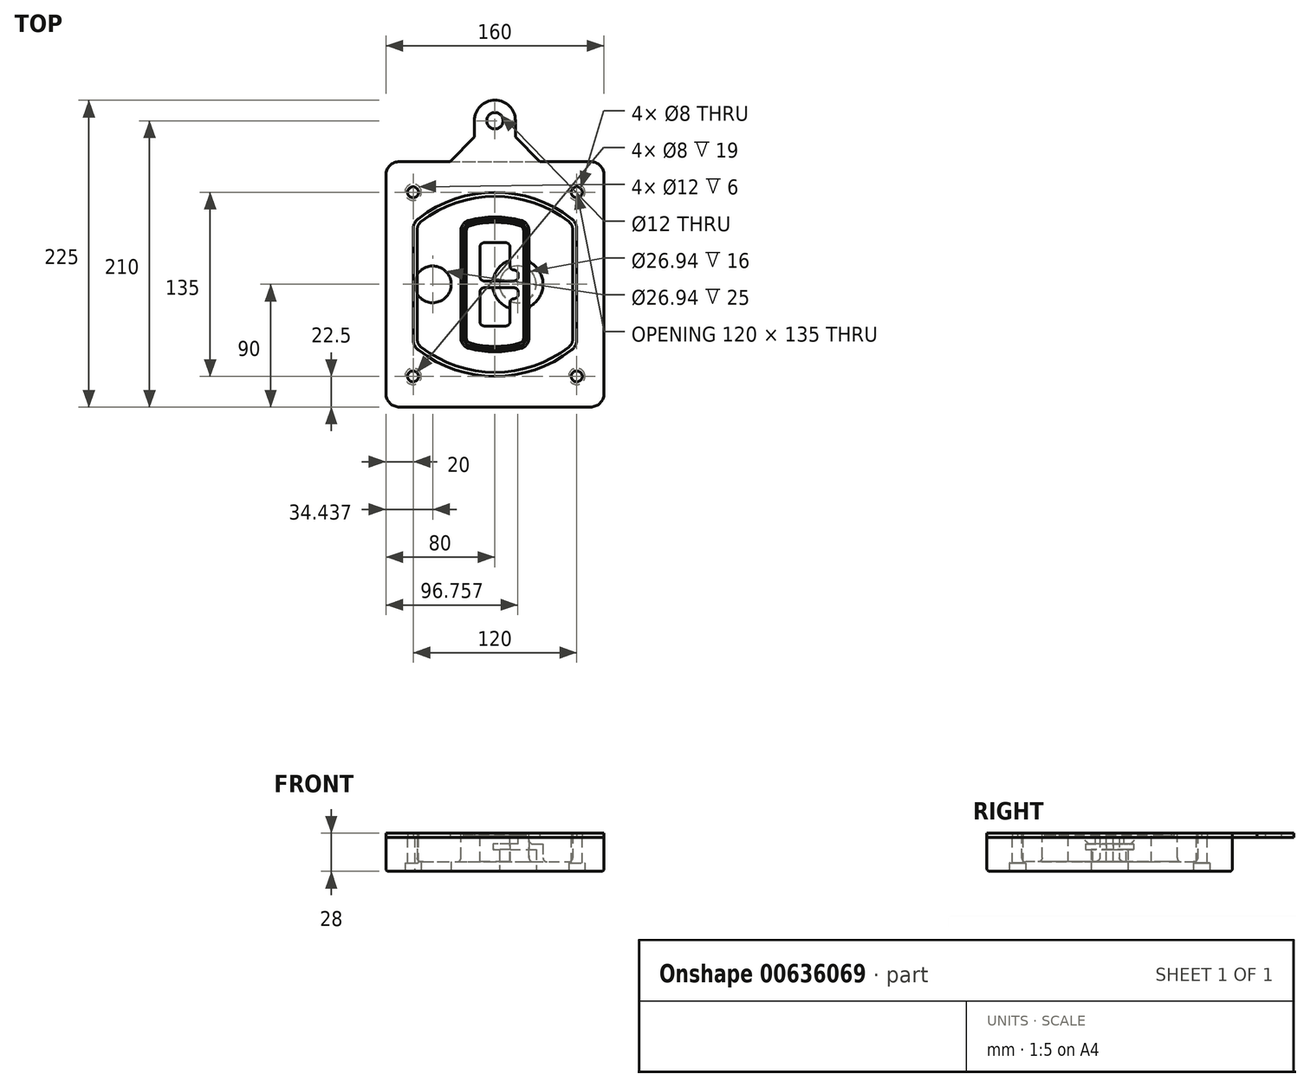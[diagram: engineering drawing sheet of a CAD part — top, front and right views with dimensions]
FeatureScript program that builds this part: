
annotation { "Feature Type Name" : "Feature", "Feature Type Description" : "" }
export const myFeature = defineFeature(function(context is Context, id is Id, definition is map)
    precondition{}
    {
        {
            var Q0;
            Q0=qCreatedBy(makeId("Top.planeOp"),FACE);
            var sketch = newSketch(context, id + "F0", { "sketchPlane" : qUnion([Q0])});
            skPoint(sketch, "E0.rect.middle", {"position": v(0, 0) * mm});
            skLineSegment(sketch, "E1.bottom", {"start": v(-70, -90) * mm, "end": v(70, -90) * mm});
            skLineSegment(sketch, "E1.top", {"start": v(-70, 90) * mm, "end": v(70, 90) * mm});
            skLineSegment(sketch, "E1.left", {"start": v(-80, -80) * mm, "end": v(-80, 80) * mm});
            skLineSegment(sketch, "E1.right", {"start": v(80, -80) * mm, "end": v(80, 80) * mm});
            skLineSegment(sketch, "E2", {"start": v(-80, 90) * mm, "end": v(80, -90) * mm, "construction": true});
            skLineSegment(sketch, "E3", {"start": v(80, 90) * mm, "end": v(-80, -90) * mm, "construction": true});
            skCircle(sketch, "E4", {"center": v(-60, 67.5) * mm, "radius": 4 * mm});
            skCircle(sketch, "E5", {"center": v(60, 67.5) * mm, "radius": 4 * mm});
            skCircle(sketch, "E6", {"center": v(60, -67.5) * mm, "radius": 4 * mm});
            skCircle(sketch, "E7", {"center": v(-60, -67.5) * mm, "radius": 4 * mm});
            skLineSegment(sketch, "E8", {"start": v(-60, 67.5) * mm, "end": v(60, 67.5) * mm, "construction": true});
            skLineSegment(sketch, "E9", {"start": v(60, 67.5) * mm, "end": v(60, -67.5) * mm, "construction": true});
            skLineSegment(sketch, "E10", {"start": v(60, -67.5) * mm, "end": v(-60, -67.5) * mm, "construction": true});
            skLineSegment(sketch, "E11", {"start": v(-60, -67.5) * mm, "end": v(-60, 67.5) * mm, "construction": true});
            skLineSegment(sketch, "E12", {"start": v(-60, 40.3) * mm, "end": v(-60, -40.3) * mm});
            skLineSegment(sketch, "E13", {"start": v(60, 40.3) * mm, "end": v(60, -40.3) * mm});
            skArc(sketch, "E14", {"start": v(56.15, 48.18) * mm, "mid": v(0, 67.5) * mm, "end": v(-56.15, 48.18) * mm});
            skArc(sketch, "E15", {"start": v(-56.15, -48.18) * mm, "mid": v(0, -67.5) * mm, "end": v(56.15, -48.18) * mm});
            skLineSegment(sketch, "E16", {"start": v(-60, 0) * mm, "end": v(60, 0) * mm, "construction": true});
            skPoint(sketch, "E17.visualSharp", {"position": v(-60, -45) * mm});
            skArc(sketch, "E17.filletArc", {"start": v(-60, -40.3) * mm, "mid": v(-58.99, -44.68) * mm, "end": v(-56.15, -48.18) * mm});
            skPoint(sketch, "E18.visualSharp", {"position": v(-60, 45) * mm});
            skArc(sketch, "E18.filletArc", {"start": v(-56.15, 48.18) * mm, "mid": v(-58.99, 44.68) * mm, "end": v(-60, 40.3) * mm});
            skPoint(sketch, "E19.visualSharp", {"position": v(60, 45) * mm});
            skArc(sketch, "E19.filletArc", {"start": v(60, 40.3) * mm, "mid": v(58.99, 44.68) * mm, "end": v(56.15, 48.18) * mm});
            skPoint(sketch, "E20.visualSharp", {"position": v(60, -45) * mm});
            skArc(sketch, "E20.filletArc", {"start": v(56.15, -48.18) * mm, "mid": v(58.99, -44.68) * mm, "end": v(60, -40.3) * mm});
            skPoint(sketch, "E21.visualSharp", {"position": v(-80, 90) * mm});
            skArc(sketch, "E21.filletArc", {"start": v(-70, 90) * mm, "mid": v(-77.07, 87.07) * mm, "end": v(-80, 80) * mm});
            skPoint(sketch, "E22.visualSharp", {"position": v(80, 90) * mm});
            skArc(sketch, "E22.filletArc", {"start": v(80, 80) * mm, "mid": v(77.07, 87.07) * mm, "end": v(70, 90) * mm});
            skPoint(sketch, "E23.visualSharp", {"position": v(80, -90) * mm});
            skArc(sketch, "E23.filletArc", {"start": v(70, -90) * mm, "mid": v(77.07, -87.07) * mm, "end": v(80, -80) * mm});
            skPoint(sketch, "E24.visualSharp", {"position": v(-80, -90) * mm});
            skArc(sketch, "E24.filletArc", {"start": v(-80, -80) * mm, "mid": v(-77.07, -87.07) * mm, "end": v(-70, -90) * mm});
            skArc(sketch, "E25.0", {"start": v(57, 40.3) * mm, "mid": v(56.3, 43.36) * mm, "end": v(54.3, 45.81) * mm});
            skLineSegment(sketch, "E25.1", {"start": v(57, 40.3) * mm, "end": v(57, -40.3) * mm});
            skArc(sketch, "E25.2", {"start": v(54.3, -45.81) * mm, "mid": v(56.3, -43.36) * mm, "end": v(57, -40.3) * mm});
            skArc(sketch, "E25.3", {"start": v(-54.3, -45.81) * mm, "mid": v(0, -64.5) * mm, "end": v(54.3, -45.81) * mm});
            skArc(sketch, "E25.4", {"start": v(-57, -40.3) * mm, "mid": v(-56.3, -43.36) * mm, "end": v(-54.3, -45.81) * mm});
            skArc(sketch, "E25.5", {"start": v(54.3, 45.81) * mm, "mid": v(0, 64.5) * mm, "end": v(-54.3, 45.81) * mm});
            skLineSegment(sketch, "E25.6", {"start": v(-57, 40.3) * mm, "end": v(-57, -40.3) * mm});
            skArc(sketch, "E25.7", {"start": v(-54.3, 45.81) * mm, "mid": v(-56.3, 43.36) * mm, "end": v(-57, 40.3) * mm});
            skArc(sketch, "E26.0", {"start": v(-58.62, 51.33) * mm, "mid": v(-62.58, 46.43) * mm, "end": v(-64, 40.3) * mm});
            skArc(sketch, "E26.1", {"start": v(58.62, 51.33) * mm, "mid": v(0, 71.5) * mm, "end": v(-58.62, 51.33) * mm});
            skArc(sketch, "E26.2", {"start": v(64, 40.3) * mm, "mid": v(62.58, 46.43) * mm, "end": v(58.62, 51.33) * mm});
            skLineSegment(sketch, "E26.3", {"start": v(64, 40.3) * mm, "end": v(64, -40.3) * mm});
            skArc(sketch, "E26.4", {"start": v(58.62, -51.33) * mm, "mid": v(62.58, -46.43) * mm, "end": v(64, -40.3) * mm});
            skLineSegment(sketch, "E26.5", {"start": v(-64, 40.3) * mm, "end": v(-64, -40.3) * mm});
            skArc(sketch, "E26.6", {"start": v(-58.62, -51.33) * mm, "mid": v(0, -71.5) * mm, "end": v(58.62, -51.33) * mm});
            skArc(sketch, "E26.7", {"start": v(-64, -40.3) * mm, "mid": v(-62.58, -46.43) * mm, "end": v(-58.62, -51.33) * mm});
            skSolve(sketch);
        }
        {
            var Q0;
            Q0=makeQuery(id+"F0.imprint","IMPRINT",FACE,{"disambiguationData":[TD([[makeQuery(id+"F0.imprint","IMPRINT",EDGE,{"derivedFrom":sQuery(id+"F0.wireOp",EDGE,"E1.bottom")}),1.0]])]});
            var Q1;
            Q1=makeQuery(id+"F0.imprint","IMPRINT",FACE,{"disambiguationData":[TD([[makeQuery(id+"F0.imprint","IMPRINT",EDGE,{"derivedFrom":sQuery(id+"F0.wireOp",EDGE,"E12")}),1.0]])]});
            var Q2;
            Q2=makeQuery(id+"F0.imprint","IMPRINT",FACE,{"disambiguationData":[TD([[makeQuery(id+"F0.imprint","IMPRINT",EDGE,{"derivedFrom":sQuery(id+"F0.wireOp",EDGE,"E25.0")}),1.0]])]});
            var Q3;
            Q3=makeQuery(id+"F0.imprint","IMPRINT",FACE,{"disambiguationData":[TD([[makeQuery(id+"F0.imprint","IMPRINT",EDGE,{"derivedFrom":sQuery(id+"F0.wireOp",EDGE,"E12")}),-1.0]])]});
            extrude(context, id + "F1", {"entities" : qUnion([Q0, Q1, Q2, Q3]), "oppositeDirection" : true, "depth" : 25 * mm});
        }
        {
            var Q0;
            Q0=makeQuery(id+"F0.imprint","IMPRINT",FACE,{"disambiguationData":[TD([[makeQuery(id+"F0.imprint","IMPRINT",EDGE,{"derivedFrom":sQuery(id+"F0.wireOp",EDGE,"E12")}),1.0]])]});
            extrude(context, id + "F2", {"entities" : qUnion([Q0]), "operationType" : NewBodyOperationType.ADD, "depth" : 3 * mm});
        }
        {
            var Q0;
            Q0=makeQuery(id+"F0.imprint","IMPRINT",FACE,{"disambiguationData":[TD([[makeQuery(id+"F0.imprint","IMPRINT",EDGE,{"derivedFrom":sQuery(id+"F0.wireOp",EDGE,"E25.0")}),1.0]])]});
            extrude(context, id + "F3", {"entities" : qUnion([Q0]), "operationType" : NewBodyOperationType.REMOVE, "oppositeDirection" : true, "depth" : 18 * mm});
        }
        {
            var Q0;
            Q0=makeQuery(id+"F2.opExtrude","CAP_FACE",FACE,{"disambiguationData":[OSD([sQuery(id+"F0.wireOp",EDGE,"E12"),sQuery(id+"F0.wireOp",EDGE,"E13"),sQuery(id+"F0.wireOp",EDGE,"E14"),sQuery(id+"F0.wireOp",EDGE,"E15"),sQuery(id+"F0.wireOp",EDGE,"E17.filletArc"),sQuery(id+"F0.wireOp",EDGE,"E18.filletArc"),sQuery(id+"F0.wireOp",EDGE,"E19.filletArc"),sQuery(id+"F0.wireOp",EDGE,"E20.filletArc"),sQuery(id+"F0.wireOp",EDGE,"E25.0"),sQuery(id+"F0.wireOp",EDGE,"E25.1"),sQuery(id+"F0.wireOp",EDGE,"E25.2"),sQuery(id+"F0.wireOp",EDGE,"E25.3"),sQuery(id+"F0.wireOp",EDGE,"E25.4"),sQuery(id+"F0.wireOp",EDGE,"E25.5"),sQuery(id+"F0.wireOp",EDGE,"E25.6"),sQuery(id+"F0.wireOp",EDGE,"E25.7")])],"isStart":false});
            var sketch = newSketch(context, id + "F4", { "sketchPlane" : qUnion([Q0])});
            skArc(sketch, "E27.0", {"start": v(-19.08, -46.97) * mm, "mid": v(0, -49.5) * mm, "end": v(19.08, -46.97) * mm});
            skArc(sketch, "E28.0", {"start": v(19.08, 46.97) * mm, "mid": v(0, 49.5) * mm, "end": v(-19.08, 46.97) * mm});
            skLineSegment(sketch, "E29", {"start": v(-25, 39.25) * mm, "end": v(-25, -39.25) * mm});
            skLineSegment(sketch, "E30", {"start": v(25, 39.25) * mm, "end": v(25, -39.25) * mm});
            skLineSegment(sketch, "E31", {"start": v(-25, 45.1) * mm, "end": v(25, 45.1) * mm, "construction": true});
            skLineSegment(sketch, "E32", {"start": v(-25, -45.1) * mm, "end": v(25, -45.1) * mm, "construction": true});
            skPoint(sketch, "E33.visualSharp", {"position": v(-25, 45.1) * mm});
            skArc(sketch, "E33.filletArc", {"start": v(-19.08, 46.97) * mm, "mid": v(-23.35, 44.11) * mm, "end": v(-25, 39.25) * mm});
            skPoint(sketch, "E34.visualSharp", {"position": v(25, 45.1) * mm});
            skArc(sketch, "E34.filletArc", {"start": v(25, 39.25) * mm, "mid": v(23.35, 44.11) * mm, "end": v(19.08, 46.97) * mm});
            skPoint(sketch, "E35.visualSharp", {"position": v(25, -45.1) * mm});
            skArc(sketch, "E35.filletArc", {"start": v(19.08, -46.97) * mm, "mid": v(23.35, -44.11) * mm, "end": v(25, -39.25) * mm});
            skPoint(sketch, "E36.visualSharp", {"position": v(-25, -45.1) * mm});
            skArc(sketch, "E36.filletArc", {"start": v(-25, -39.25) * mm, "mid": v(-23.35, -44.11) * mm, "end": v(-19.08, -46.97) * mm});
            skArc(sketch, "E37.0", {"start": v(54.3, 45.81) * mm, "mid": v(0, 64.5) * mm, "end": v(-54.3, 45.81) * mm});
            skArc(sketch, "E37.1", {"start": v(-54.3, 45.81) * mm, "mid": v(-56.3, 43.36) * mm, "end": v(-57, 40.3) * mm});
            skLineSegment(sketch, "E37.2", {"start": v(-57, 40.3) * mm, "end": v(-57, -40.3) * mm});
            skArc(sketch, "E37.3", {"start": v(-57, -40.3) * mm, "mid": v(-56.3, -43.36) * mm, "end": v(-54.3, -45.81) * mm});
            skArc(sketch, "E37.4", {"start": v(-54.3, -45.81) * mm, "mid": v(0, -64.5) * mm, "end": v(54.3, -45.81) * mm});
            skArc(sketch, "E37.5", {"start": v(54.3, -45.81) * mm, "mid": v(56.3, -43.36) * mm, "end": v(57, -40.3) * mm});
            skLineSegment(sketch, "E37.6", {"start": v(57, 40.3) * mm, "end": v(57, -40.3) * mm});
            skArc(sketch, "E37.7", {"start": v(57, 40.3) * mm, "mid": v(56.3, 43.36) * mm, "end": v(54.3, 45.81) * mm});
            skLineSegment(sketch, "E38.0", {"start": v(23, 39.25) * mm, "end": v(23, -39.25) * mm});
            skArc(sketch, "E38.1", {"start": v(18.56, -45.04) * mm, "mid": v(21.76, -42.9) * mm, "end": v(23, -39.25) * mm});
            skArc(sketch, "E38.2", {"start": v(-18.56, -45.04) * mm, "mid": v(0, -47.5) * mm, "end": v(18.56, -45.04) * mm});
            skArc(sketch, "E38.3", {"start": v(-23, -39.25) * mm, "mid": v(-21.76, -42.9) * mm, "end": v(-18.56, -45.04) * mm});
            skLineSegment(sketch, "E38.4", {"start": v(-23, 39.25) * mm, "end": v(-23, -39.25) * mm});
            skArc(sketch, "E38.5", {"start": v(23, 39.25) * mm, "mid": v(21.76, 42.9) * mm, "end": v(18.56, 45.04) * mm});
            skArc(sketch, "E38.6", {"start": v(-18.56, 45.04) * mm, "mid": v(-21.76, 42.9) * mm, "end": v(-23, 39.25) * mm});
            skArc(sketch, "E38.7", {"start": v(18.56, 45.04) * mm, "mid": v(0, 47.5) * mm, "end": v(-18.56, 45.04) * mm});
            skArc(sketch, "E39.0", {"start": v(21, 39.25) * mm, "mid": v(20.18, 41.68) * mm, "end": v(18.04, 43.1) * mm});
            skLineSegment(sketch, "E39.1", {"start": v(21, 39.25) * mm, "end": v(21, -39.25) * mm});
            skArc(sketch, "E39.2", {"start": v(18.04, -43.1) * mm, "mid": v(20.18, -41.68) * mm, "end": v(21, -39.25) * mm});
            skArc(sketch, "E39.3", {"start": v(-18.04, -43.1) * mm, "mid": v(0, -45.5) * mm, "end": v(18.04, -43.1) * mm});
            skArc(sketch, "E39.4", {"start": v(-21, -39.25) * mm, "mid": v(-20.18, -41.68) * mm, "end": v(-18.04, -43.1) * mm});
            skArc(sketch, "E39.5", {"start": v(18.04, 43.1) * mm, "mid": v(0, 45.5) * mm, "end": v(-18.04, 43.1) * mm});
            skLineSegment(sketch, "E39.6", {"start": v(-21, 39.25) * mm, "end": v(-21, -39.25) * mm});
            skArc(sketch, "E39.7", {"start": v(-18.04, 43.1) * mm, "mid": v(-20.18, 41.68) * mm, "end": v(-21, 39.25) * mm});
            skLineSegment(sketch, "E40", {"start": v(-25, 0) * mm, "end": v(25, 0) * mm, "construction": true});
            skLineSegment(sketch, "E41", {"start": v(-11, 5.5) * mm, "end": v(-11, 27.5) * mm});
            skLineSegment(sketch, "E42", {"start": v(-8, 30.5) * mm, "end": v(8, 30.5) * mm});
            skLineSegment(sketch, "E43", {"start": v(11, 27.5) * mm, "end": v(11, 13.5) * mm});
            skLineSegment(sketch, "E44", {"start": v(14, 10.5) * mm, "end": v(14, 10.5) * mm});
            skLineSegment(sketch, "E45", {"start": v(17, 7.5) * mm, "end": v(17, 5.5) * mm});
            skLineSegment(sketch, "E46", {"start": v(14, 2.5) * mm, "end": v(-8, 2.5) * mm});
            skPoint(sketch, "E47.visualSharp", {"position": v(-11, 30.5) * mm});
            skArc(sketch, "E47.filletArc", {"start": v(-8, 30.5) * mm, "mid": v(-10.12, 29.62) * mm, "end": v(-11, 27.5) * mm});
            skPoint(sketch, "E48.visualSharp", {"position": v(11, 30.5) * mm});
            skArc(sketch, "E48.filletArc", {"start": v(11, 27.5) * mm, "mid": v(10.12, 29.62) * mm, "end": v(8, 30.5) * mm});
            skPoint(sketch, "E49.visualSharp", {"position": v(11, 10.5) * mm});
            skArc(sketch, "E49.filletArc", {"start": v(11, 13.5) * mm, "mid": v(11.88, 11.38) * mm, "end": v(14, 10.5) * mm});
            skPoint(sketch, "E50.visualSharp", {"position": v(17, 10.5) * mm});
            skArc(sketch, "E50.filletArc", {"start": v(17, 7.5) * mm, "mid": v(16.12, 9.62) * mm, "end": v(14, 10.5) * mm});
            skPoint(sketch, "E51.visualSharp", {"position": v(17, 2.5) * mm});
            skArc(sketch, "E51.filletArc", {"start": v(14, 2.5) * mm, "mid": v(16.12, 3.38) * mm, "end": v(17, 5.5) * mm});
            skPoint(sketch, "E52.visualSharp", {"position": v(-11, 2.5) * mm});
            skArc(sketch, "E52.filletArc", {"start": v(-11, 5.5) * mm, "mid": v(-10.12, 3.38) * mm, "end": v(-8, 2.5) * mm});
            skLineSegment(sketch, "E53.0.MirrorCS", {"start": v(14, -2.5) * mm, "end": v(-8, -2.5) * mm});
            skArc(sketch, "E54.0.MirrorCS", {"start": v(-11, -5.5) * mm, "mid": v(-10.12, -3.38) * mm, "end": v(-8, -2.5) * mm});
            skLineSegment(sketch, "E55.0.MirrorCS", {"start": v(-11, -5.5) * mm, "end": v(-11, -27.5) * mm});
            skArc(sketch, "E56.0.MirrorCS", {"start": v(-8, -30.5) * mm, "mid": v(-10.12, -29.62) * mm, "end": v(-11, -27.5) * mm});
            skLineSegment(sketch, "E57.0.MirrorCS", {"start": v(-8, -30.5) * mm, "end": v(8, -30.5) * mm});
            skArc(sketch, "E58.0.MirrorCS", {"start": v(11, -27.5) * mm, "mid": v(10.12, -29.62) * mm, "end": v(8, -30.5) * mm});
            skLineSegment(sketch, "E59.0.MirrorCS", {"start": v(11, -27.5) * mm, "end": v(11, -13.5) * mm});
            skArc(sketch, "E60.0.MirrorCS", {"start": v(11, -13.5) * mm, "mid": v(11.88, -11.38) * mm, "end": v(14, -10.5) * mm});
            skArc(sketch, "E61.0.MirrorCS", {"start": v(17, -7.5) * mm, "mid": v(16.12, -9.62) * mm, "end": v(14, -10.5) * mm});
            skLineSegment(sketch, "E62.0.MirrorCS", {"start": v(17, -7.5) * mm, "end": v(17, -5.5) * mm});
            skArc(sketch, "E63.0.MirrorCS", {"start": v(14, -2.5) * mm, "mid": v(16.12, -3.38) * mm, "end": v(17, -5.5) * mm});
            skSolve(sketch);
        }
        {
            var Q0;
            Q0=makeQuery(id+"F4.imprint","IMPRINT",FACE,{"disambiguationData":[TD([[makeQuery(id+"F4.imprint","IMPRINT",EDGE,{"derivedFrom":sQuery(id+"F4.wireOp",EDGE,"E27.0")}),1.0]])]});
            var Q1;
            Q1=makeQuery(id+"F4.imprint","IMPRINT",FACE,{"disambiguationData":[TD([[makeQuery(id+"F4.imprint","IMPRINT",EDGE,{"derivedFrom":sQuery(id+"F4.wireOp",EDGE,"E38.0")}),-1.0]])]});
            var Q2;
            Q2=makeQuery(id+"F4.imprint","IMPRINT",FACE,{"disambiguationData":[TD([[makeQuery(id+"F4.imprint","IMPRINT",EDGE,{"derivedFrom":sQuery(id+"F4.wireOp",EDGE,"E39.0")}),1.0]])]});
            extrude(context, id + "F5", {"entities" : qUnion([Q0, Q1, Q2]), "operationType" : NewBodyOperationType.ADD, "endBound" : BoundingType.UP_TO_NEXT, "oppositeDirection" : true, "depth" : 25 * mm});
        }
        {
            var Q0;
            Q0=makeQuery(id+"F4.imprint","IMPRINT",FACE,{"disambiguationData":[TD([[makeQuery(id+"F4.imprint","IMPRINT",EDGE,{"derivedFrom":sQuery(id+"F4.wireOp",EDGE,"E38.0")}),-1.0]])]});
            extrude(context, id + "F6", {"entities" : qUnion([Q0]), "operationType" : NewBodyOperationType.REMOVE, "oppositeDirection" : true, "depth" : 2 * mm});
        }
        {
            var Q0;
            Q0=makeQuery(id+"F1.opExtrude","CAP_FACE",FACE,{"disambiguationData":[OSD([sQuery(id+"F0.wireOp",EDGE,"E1.bottom"),sQuery(id+"F0.wireOp",EDGE,"E1.top"),sQuery(id+"F0.wireOp",EDGE,"E1.left"),sQuery(id+"F0.wireOp",EDGE,"E1.right"),sQuery(id+"F0.wireOp",EDGE,"E4"),sQuery(id+"F0.wireOp",EDGE,"E5"),sQuery(id+"F0.wireOp",EDGE,"E6"),sQuery(id+"F0.wireOp",EDGE,"E7"),sQuery(id+"F0.wireOp",EDGE,"E21.filletArc"),sQuery(id+"F0.wireOp",EDGE,"E22.filletArc"),sQuery(id+"F0.wireOp",EDGE,"E23.filletArc"),sQuery(id+"F0.wireOp",EDGE,"E24.filletArc")])],"isStart":false});
            var sketch = newSketch(context, id + "F7", { "sketchPlane" : qUnion([Q0])});
            skCircle(sketch, "E64", {"center": v(16.76, 0) * mm, "radius": 13.47 * mm});
            skCircle(sketch, "E65", {"center": v(-45.56, 0) * mm, "radius": 13.47 * mm});
            skLineSegment(sketch, "E66", {"start": v(80, 0) * mm, "end": v(-80, 0) * mm});
            skCircle(sketch, "E67", {"center": v(16.76, 0) * mm, "radius": 18.47 * mm});
            skCircle(sketch, "E68", {"center": v(60, -67.5) * mm, "radius": 6 * mm});
            skCircle(sketch, "E69", {"center": v(-60, -67.5) * mm, "radius": 6 * mm});
            skCircle(sketch, "E70", {"center": v(-60, 67.5) * mm, "radius": 6 * mm});
            skCircle(sketch, "E71", {"center": v(60, 67.5) * mm, "radius": 6 * mm});
            skSolve(sketch);
        }
        {
            var Q0;
            {var subQ1=sQuery(id+"F7.wireOp",EDGE,"E66");var subQ4=sQuery(id+"F7.wireOp",EDGE,"E64");var subQ6=makeQuery(id+"F7.imprint","INTERSECT",VERTEX,{"disambiguationData":[OD(0.0)],"derivedFrom":[subQ4,subQ1]});Q0=makeQuery(id+"F7.imprint","IMPRINT",FACE,{"disambiguationData":[TD([[makeQuery(id+"F7.imprint","IMPRINT",EDGE,{"disambiguationData":[TD([[subQ6,-1.0]])],"derivedFrom":subQ4}),-1.0]])]});}
            var Q1;
            {var subQ0=sQuery(id+"F7.wireOp",EDGE,"E66");var subQ1=sQuery(id+"F7.wireOp",EDGE,"E64");var subQ3=makeQuery(id+"F7.imprint","INTERSECT",VERTEX,{"disambiguationData":[OD(0.0)],"derivedFrom":[subQ1,subQ0]});Q1=makeQuery(id+"F7.imprint","IMPRINT",FACE,{"disambiguationData":[TD([[makeQuery(id+"F7.imprint","IMPRINT",EDGE,{"disambiguationData":[TD([[subQ3,-1.0]])],"derivedFrom":subQ1}),1.0]])]});}
            var Q2;
            {var subQ0=sQuery(id+"F7.wireOp",EDGE,"E66");var subQ1=sQuery(id+"F7.wireOp",EDGE,"E64");var subQ3=makeQuery(id+"F7.imprint","INTERSECT",VERTEX,{"disambiguationData":[OD(0.0)],"derivedFrom":[subQ1,subQ0]});Q2=makeQuery(id+"F7.imprint","IMPRINT",FACE,{"disambiguationData":[TD([[makeQuery(id+"F7.imprint","IMPRINT",EDGE,{"disambiguationData":[TD([[subQ3,1.0]])],"derivedFrom":subQ1}),1.0]])]});}
            var Q3;
            {var subQ1=sQuery(id+"F7.wireOp",EDGE,"E66");var subQ4=sQuery(id+"F7.wireOp",EDGE,"E64");var subQ6=makeQuery(id+"F7.imprint","INTERSECT",VERTEX,{"disambiguationData":[OD(0.0)],"derivedFrom":[subQ4,subQ1]});Q3=makeQuery(id+"F7.imprint","IMPRINT",FACE,{"disambiguationData":[TD([[makeQuery(id+"F7.imprint","IMPRINT",EDGE,{"disambiguationData":[TD([[subQ6,1.0]])],"derivedFrom":subQ4}),-1.0]])]});}
            extrude(context, id + "F8", {"entities" : qUnion([Q0, Q1, Q2, Q3]), "operationType" : NewBodyOperationType.ADD, "oppositeDirection" : true, "depth" : 20 * mm});
        }
        {
            var Q0;
            {var subQ0=sQuery(id+"F7.wireOp",EDGE,"E66");var subQ1=sQuery(id+"F7.wireOp",EDGE,"E64");var subQ3=makeQuery(id+"F7.imprint","INTERSECT",VERTEX,{"disambiguationData":[OD(0.0)],"derivedFrom":[subQ1,subQ0]});Q0=makeQuery(id+"F7.imprint","IMPRINT",FACE,{"disambiguationData":[TD([[makeQuery(id+"F7.imprint","IMPRINT",EDGE,{"disambiguationData":[TD([[subQ3,-1.0]])],"derivedFrom":subQ1}),1.0]])]});}
            var Q1;
            {var subQ0=sQuery(id+"F7.wireOp",EDGE,"E66");var subQ1=sQuery(id+"F7.wireOp",EDGE,"E64");var subQ3=makeQuery(id+"F7.imprint","INTERSECT",VERTEX,{"disambiguationData":[OD(0.0)],"derivedFrom":[subQ1,subQ0]});Q1=makeQuery(id+"F7.imprint","IMPRINT",FACE,{"disambiguationData":[TD([[makeQuery(id+"F7.imprint","IMPRINT",EDGE,{"disambiguationData":[TD([[subQ3,1.0]])],"derivedFrom":subQ1}),1.0]])]});}
            extrude(context, id + "F9", {"entities" : qUnion([Q0, Q1]), "operationType" : NewBodyOperationType.REMOVE, "oppositeDirection" : true, "depth" : 16 * mm});
        }
        {
            var Q0;
            {var subQ0=sQuery(id+"F7.wireOp",EDGE,"E66");var subQ1=sQuery(id+"F7.wireOp",EDGE,"E65");var subQ3=makeQuery(id+"F7.imprint","INTERSECT",VERTEX,{"disambiguationData":[OD(0.0)],"derivedFrom":[subQ1,subQ0]});Q0=makeQuery(id+"F7.imprint","IMPRINT",FACE,{"disambiguationData":[TD([[makeQuery(id+"F7.imprint","IMPRINT",EDGE,{"disambiguationData":[TD([[subQ3,-1.0]])],"derivedFrom":subQ1}),1.0]])]});}
            var Q1;
            {var subQ0=sQuery(id+"F7.wireOp",EDGE,"E66");var subQ1=sQuery(id+"F7.wireOp",EDGE,"E65");var subQ3=makeQuery(id+"F7.imprint","INTERSECT",VERTEX,{"disambiguationData":[OD(0.0)],"derivedFrom":[subQ1,subQ0]});Q1=makeQuery(id+"F7.imprint","IMPRINT",FACE,{"disambiguationData":[TD([[makeQuery(id+"F7.imprint","IMPRINT",EDGE,{"disambiguationData":[TD([[subQ3,1.0]])],"derivedFrom":subQ1}),1.0]])]});}
            extrude(context, id + "F10", {"entities" : qUnion([Q0, Q1]), "operationType" : NewBodyOperationType.REMOVE, "oppositeDirection" : true, "depth" : 25 * mm});
        }
        {
            var Q0;
            Q0=makeQuery(id+"F7.imprint","IMPRINT",FACE,{"disambiguationData":[TD([[makeQuery(id+"F7.imprint","IMPRINT",EDGE,{"derivedFrom":sQuery(id+"F7.wireOp",EDGE,"E68")}),1.0]])]});
            var Q1;
            Q1=makeQuery(id+"F7.imprint","IMPRINT",FACE,{"disambiguationData":[TD([[makeQuery(id+"F7.imprint","IMPRINT",EDGE,{"derivedFrom":makeQuery(id+"F1.opExtrude","CAP_EDGE",EDGE,{"disambiguationData":[OSD([sQuery(id+"F0.wireOp",EDGE,"E5")])],"isStart":false})}),-1.0]])]});
            var Q2;
            Q2=makeQuery(id+"F7.imprint","IMPRINT",FACE,{"disambiguationData":[TD([[makeQuery(id+"F7.imprint","IMPRINT",EDGE,{"derivedFrom":sQuery(id+"F7.wireOp",EDGE,"E69")}),1.0]])]});
            var Q3;
            Q3=makeQuery(id+"F7.imprint","IMPRINT",FACE,{"disambiguationData":[TD([[makeQuery(id+"F7.imprint","IMPRINT",EDGE,{"derivedFrom":makeQuery(id+"F1.opExtrude","CAP_EDGE",EDGE,{"disambiguationData":[OSD([sQuery(id+"F0.wireOp",EDGE,"E4")])],"isStart":false})}),-1.0]])]});
            var Q4;
            Q4=makeQuery(id+"F7.imprint","IMPRINT",FACE,{"disambiguationData":[TD([[makeQuery(id+"F7.imprint","IMPRINT",EDGE,{"derivedFrom":sQuery(id+"F7.wireOp",EDGE,"E70")}),1.0]])]});
            var Q5;
            Q5=makeQuery(id+"F7.imprint","IMPRINT",FACE,{"disambiguationData":[TD([[makeQuery(id+"F7.imprint","IMPRINT",EDGE,{"derivedFrom":makeQuery(id+"F1.opExtrude","CAP_EDGE",EDGE,{"disambiguationData":[OSD([sQuery(id+"F0.wireOp",EDGE,"E7")])],"isStart":false})}),-1.0]])]});
            var Q6;
            Q6=makeQuery(id+"F7.imprint","IMPRINT",FACE,{"disambiguationData":[TD([[makeQuery(id+"F7.imprint","IMPRINT",EDGE,{"derivedFrom":sQuery(id+"F7.wireOp",EDGE,"E71")}),1.0]])]});
            var Q7;
            Q7=makeQuery(id+"F7.imprint","IMPRINT",FACE,{"disambiguationData":[TD([[makeQuery(id+"F7.imprint","IMPRINT",EDGE,{"derivedFrom":makeQuery(id+"F1.opExtrude","CAP_EDGE",EDGE,{"disambiguationData":[OSD([sQuery(id+"F0.wireOp",EDGE,"E6")])],"isStart":false})}),-1.0]])]});
            extrude(context, id + "F11", {"entities" : qUnion([Q0, Q1, Q2, Q3, Q4, Q5, Q6, Q7]), "operationType" : NewBodyOperationType.REMOVE, "oppositeDirection" : true, "depth" : 6 * mm});
        }
        {
            var Q0;
            Q0=makeQuery(id+"F9.boolean.opBoolean","COPY",FACE,{"derivedFrom":makeQuery(id+"F9.opExtrude","CAP_FACE",FACE,{"disambiguationData":[OSD([sQuery(id+"F7.wireOp",EDGE,"E64")])],"isStart":false})});
            var sketch = newSketch(context, id + "F12", { "sketchPlane" : qUnion([Q0])});
            skArc(sketch, "E72.0", {"start": v(11, 17.55) * mm, "mid": v(2.57, 11.82) * mm, "end": v(-1.54, 2.5) * mm});
            skArc(sketch, "E72.1", {"start": v(-1.54, -2.5) * mm, "mid": v(2.57, -11.82) * mm, "end": v(11, -17.55) * mm});
            skLineSegment(sketch, "E73", {"start": v(-1.54, -2.5) * mm, "end": v(14, -2.5) * mm});
            skLineSegment(sketch, "E74.0", {"start": v(14, 2.5) * mm, "end": v(-1.54, 2.5) * mm});
            skArc(sketch, "E74.1", {"start": v(14, 2.5) * mm, "mid": v(16.12, 3.38) * mm, "end": v(17, 5.5) * mm});
            skLineSegment(sketch, "E74.2", {"start": v(17, 7.5) * mm, "end": v(17, 5.5) * mm});
            skArc(sketch, "E74.3", {"start": v(17, 7.5) * mm, "mid": v(16.12, 9.62) * mm, "end": v(14, 10.5) * mm});
            skArc(sketch, "E74.4", {"start": v(11, 13.5) * mm, "mid": v(11.88, 11.38) * mm, "end": v(14, 10.5) * mm});
            skLineSegment(sketch, "E74.5", {"start": v(11, 17.55) * mm, "end": v(11, 13.5) * mm});
            skLineSegment(sketch, "E74.7", {"start": v(14, -2.5) * mm, "end": v(-1.54, -2.5) * mm});
            skArc(sketch, "E74.8", {"start": v(14, -2.5) * mm, "mid": v(16.12, -3.38) * mm, "end": v(17, -5.5) * mm});
            skLineSegment(sketch, "E74.9", {"start": v(17, -7.5) * mm, "end": v(17, -5.5) * mm});
            skArc(sketch, "E74.10", {"start": v(17, -7.5) * mm, "mid": v(16.12, -9.62) * mm, "end": v(14, -10.5) * mm});
            skArc(sketch, "E74.11", {"start": v(11, -13.5) * mm, "mid": v(11.88, -11.38) * mm, "end": v(14, -10.5) * mm});
            skLineSegment(sketch, "E74.12", {"start": v(11, -17.55) * mm, "end": v(11, -13.5) * mm});
            skPoint(sketch, "E75.orphan", {"position": v(11, -27.5) * mm});
            skPoint(sketch, "E76.orphan", {"position": v(-8, -2.5) * mm});
            skPoint(sketch, "E77.orphan", {"position": v(-8, 2.5) * mm});
            skPoint(sketch, "E78.orphan", {"position": v(11, 27.5) * mm});
            skSolve(sketch);
        }
        {
            var Q0;
            {var subQ7=sQuery(id+"F12.wireOp",EDGE,"E72.0");var subQ14=sQuery(id+"F12.wireOp",EDGE,"E72.1");var subQ16=sQuery(id+"F12.wireOp",EDGE,"E74.1");var subQ18=sQuery(id+"F12.wireOp",EDGE,"E74.8");Q0=qUnion([makeQuery(id+"F12.imprint","IMPRINT",FACE,{"disambiguationData":[TD([[makeQuery(id+"F12.imprint","IMPRINT",EDGE,{"derivedFrom":subQ7}),1.0]])]}),makeQuery(id+"F12.imprint","IMPRINT",FACE,{"disambiguationData":[TD([[makeQuery(id+"F12.imprint","IMPRINT",EDGE,{"derivedFrom":subQ14}),1.0]])]}),makeQuery(id+"F12.imprint","IMPRINT",FACE,{"disambiguationData":[TD([[makeQuery(id+"F12.imprint","IMPRINT",EDGE,{"derivedFrom":subQ16}),1.0]])]}),makeQuery(id+"F12.imprint","IMPRINT",FACE,{"disambiguationData":[TD([[makeQuery(id+"F12.imprint","IMPRINT",EDGE,{"derivedFrom":subQ18}),-1.0]])]})]);}
            var Q1;
            Q1=makeQuery(id+"F5.boolean.opBoolean","SPLIT",FACE,{"disambiguationData":[TD([makeQuery(id+"F5.opExtrude","SWEPT_FACE",FACE,{"disambiguationData":[OSD([sQuery(id+"F4.wireOp",EDGE,"E41")])]})])],"derivedFrom":makeQuery(id+"F3.boolean.opBoolean","COPY",FACE,{"derivedFrom":makeQuery(id+"F3.opExtrude","CAP_FACE",FACE,{"disambiguationData":[OSD([sQuery(id+"F0.wireOp",EDGE,"E25.0"),sQuery(id+"F0.wireOp",EDGE,"E25.1"),sQuery(id+"F0.wireOp",EDGE,"E25.2"),sQuery(id+"F0.wireOp",EDGE,"E25.3"),sQuery(id+"F0.wireOp",EDGE,"E25.4"),sQuery(id+"F0.wireOp",EDGE,"E25.5"),sQuery(id+"F0.wireOp",EDGE,"E25.6"),sQuery(id+"F0.wireOp",EDGE,"E25.7")])],"isStart":false})})});
            extrude(context, id + "F13", {"entities" : qUnion([Q0]), "operationType" : NewBodyOperationType.REMOVE, "endBound" : BoundingType.UP_TO_SURFACE, "endBoundEntityFace" : qUnion([Q1]), "depth" : 25 * mm});
        }
        {
            var Q0;
            Q0=makeQuery(id+"F3.boolean.opBoolean","COPY",EDGE,{"derivedFrom":makeQuery(id+"F3.opExtrude","CAP_EDGE",EDGE,{"disambiguationData":[OSD([sQuery(id+"F0.wireOp",EDGE,"E25.6")])],"isStart":false})});
            var Q1;
            Q1=makeQuery(id+"F8.boolean.opBoolean","INTERSECT",EDGE,{"derivedFrom":[makeQuery(id+"F5.opExtrude","SWEPT_FACE",FACE,{"disambiguationData":[OSD([sQuery(id+"F4.wireOp",EDGE,"E30")])]}),makeQuery(id+"F8.opExtrude","CAP_FACE",FACE,{"disambiguationData":[OSD([sQuery(id+"F7.wireOp",EDGE,"E67")])],"isStart":false})]});
            var Q2;
            Q2=makeQuery(id+"F8.boolean.opBoolean","INTERSECT",EDGE,{"disambiguationData":[OD(1.0)],"derivedFrom":[makeQuery(id+"F5.opExtrude","SWEPT_FACE",FACE,{"disambiguationData":[OSD([sQuery(id+"F4.wireOp",EDGE,"E30")])]}),makeQuery(id+"F8.opExtrude","SWEPT_FACE",FACE,{"disambiguationData":[OSD([sQuery(id+"F7.wireOp",EDGE,"E67")])]})]});
            var Q3;
            {var subQ0=sQuery(id+"F4.wireOp",EDGE,"E30");Q3=makeQuery(id+"F8.boolean.opBoolean","SPLIT",EDGE,{"disambiguationData":[TD([makeQuery(id+"F5.opExtrude","SWEPT_FACE",FACE,{"disambiguationData":[OSD([sQuery(id+"F4.wireOp",EDGE,"E35.filletArc")])]})])],"derivedFrom":makeQuery(id+"F5.opExtrude","CAP_EDGE",EDGE,{"disambiguationData":[OSD([subQ0])],"isStart":false})});}
            var Q4;
            {var subQ0=sQuery(id+"F0.wireOp",EDGE,"E25.7");var subQ1=sQuery(id+"F0.wireOp",EDGE,"E25.1");var subQ2=sQuery(id+"F0.wireOp",EDGE,"E25.6");var subQ3=sQuery(id+"F0.wireOp",EDGE,"E25.5");var subQ4=sQuery(id+"F0.wireOp",EDGE,"E25.4");var subQ5=sQuery(id+"F0.wireOp",EDGE,"E25.0");var subQ6=sQuery(id+"F0.wireOp",EDGE,"E25.2");var subQ7=sQuery(id+"F0.wireOp",EDGE,"E25.3");Q4=makeQuery(id+"F8.boolean.opBoolean","INTERSECT",EDGE,{"derivedFrom":[makeQuery(id+"F5.boolean.opBoolean","SPLIT",FACE,{"disambiguationData":[TD([makeQuery(id+"F2.opExtrude","SWEPT_FACE",FACE,{"disambiguationData":[OSD([subQ5])]})])],"derivedFrom":makeQuery(id+"F3.boolean.opBoolean","COPY",FACE,{"derivedFrom":makeQuery(id+"F3.opExtrude","CAP_FACE",FACE,{"disambiguationData":[OSD([subQ5,subQ1,subQ6,subQ7,subQ4,subQ3,subQ2,subQ0])],"isStart":false})})}),makeQuery(id+"F8.opExtrude","SWEPT_FACE",FACE,{"disambiguationData":[OSD([sQuery(id+"F7.wireOp",EDGE,"E67")])]})]});}
            var Q5;
            Q5=makeQuery(id+"F8.boolean.opBoolean","INTERSECT",EDGE,{"disambiguationData":[OD(0.0)],"derivedFrom":[makeQuery(id+"F5.opExtrude","SWEPT_FACE",FACE,{"disambiguationData":[OSD([sQuery(id+"F4.wireOp",EDGE,"E30")])]}),makeQuery(id+"F8.opExtrude","SWEPT_FACE",FACE,{"disambiguationData":[OSD([sQuery(id+"F7.wireOp",EDGE,"E67")])]})]});
            fillet(context, id + "F14", {"entities" : qUnion([Q0, Q1, Q2, Q3, Q4, Q5]), "radius" : 3 * mm, "tangentPropagation" : true, "allowEdgeOverflow" : false});
        }
        {
            var Q0;
            Q0=makeQuery(id+"F1.opExtrude","CAP_EDGE",EDGE,{"disambiguationData":[OSD([sQuery(id+"F0.wireOp",EDGE,"E1.bottom")])],"isStart":false});
            fillet(context, id + "F15", {"entities" : qUnion([Q0]), "radius" : 2 * mm, "tangentPropagation" : true, "allowEdgeOverflow" : false});
        }
        {
            var Q0;
            {var subQ0=sQuery(id+"F0.wireOp",EDGE,"E21.filletArc");var subQ1=sQuery(id+"F0.wireOp",EDGE,"E7");var subQ2=sQuery(id+"F0.wireOp",EDGE,"E6");var subQ3=sQuery(id+"F0.wireOp",EDGE,"E5");var subQ4=sQuery(id+"F0.wireOp",EDGE,"E4");var subQ5=sQuery(id+"F0.wireOp",EDGE,"E22.filletArc");var subQ6=sQuery(id+"F0.wireOp",EDGE,"E1.bottom");var subQ7=sQuery(id+"F0.wireOp",EDGE,"E1.right");var subQ8=sQuery(id+"F0.wireOp",EDGE,"E1.top");var subQ9=sQuery(id+"F0.wireOp",EDGE,"E1.left");var subQ10=sQuery(id+"F0.wireOp",EDGE,"E23.filletArc");var subQ11=sQuery(id+"F0.wireOp",EDGE,"E24.filletArc");Q0=makeQuery(id+"F2.boolean.opBoolean","SPLIT",FACE,{"disambiguationData":[TD([makeQuery(id+"F1.opExtrude","SWEPT_FACE",FACE,{"disambiguationData":[OSD([subQ6])]})])],"derivedFrom":makeQuery(id+"F1.opExtrude","CAP_FACE",FACE,{"disambiguationData":[OSD([subQ6,subQ8,subQ9,subQ7,subQ4,subQ3,subQ2,subQ1,subQ0,subQ5,subQ10,subQ11])],"isStart":true})});}
            var sketch = newSketch(context, id + "F16", { "sketchPlane" : qUnion([Q0])});
            skCircle(sketch, "E79", {"center": v(0, 120) * mm, "radius": 6 * mm});
            skArc(sketch, "E80", {"start": v(15, 120) * mm, "mid": v(0, 135) * mm, "end": v(-15, 120) * mm});
            skLineSegment(sketch, "E81", {"start": v(-15, 120) * mm, "end": v(-15, 108) * mm});
            skLineSegment(sketch, "E82", {"start": v(-15, 108) * mm, "end": v(-33, 90) * mm});
            skLineSegment(sketch, "E83", {"start": v(15, 120) * mm, "end": v(15, 108) * mm});
            skLineSegment(sketch, "E84", {"start": v(15, 108) * mm, "end": v(33, 90) * mm});
            skLineSegment(sketch, "E85", {"start": v(0, 120) * mm, "end": v(0, 90) * mm, "construction": true});
            skLineSegment(sketch, "E86", {"start": v(-117.7, 0) * mm, "end": v(137.66, 0) * mm, "construction": true});
            skPoint(sketch, "E86.startSnap0", {"position": v(-80, 0) * mm});
            skArc(sketch, "E87.MirrorCS", {"start": v(15, -120) * mm, "mid": v(0, -135) * mm, "end": v(-15, -120) * mm});
            skLineSegment(sketch, "E88.MirrorCS", {"start": v(-15, -120) * mm, "end": v(-15, -108) * mm});
            skLineSegment(sketch, "E89.MirrorCS", {"start": v(-15, -108) * mm, "end": v(-33, -90) * mm});
            skCircle(sketch, "E90.MirrorC", {"center": v(0, -120) * mm, "radius": 6 * mm});
            skLineSegment(sketch, "E91.MirrorCS", {"start": v(15, -120) * mm, "end": v(15, -108) * mm});
            skLineSegment(sketch, "E92.MirrorCS", {"start": v(15, -108) * mm, "end": v(33, -90) * mm});
            skLineSegment(sketch, "E93.0", {"start": v(-80, -80) * mm, "end": v(-80, 80) * mm});
            skArc(sketch, "E94.0", {"start": v(-70, 90) * mm, "mid": v(-77.07, 87.07) * mm, "end": v(-80, 80) * mm});
            skLineSegment(sketch, "E95.0.0", {"start": v(70, 90) * mm, "end": v(-70, 90) * mm});
            skLineSegment(sketch, "E95.0.2", {"start": v(-80, 80) * mm, "end": v(-80, -80) * mm});
            skArc(sketch, "E95.0.3", {"start": v(-80, -80) * mm, "mid": v(-77.07, -87.07) * mm, "end": v(-70, -90) * mm});
            skLineSegment(sketch, "E95.0.4", {"start": v(-70, -90) * mm, "end": v(70, -90) * mm});
            skArc(sketch, "E95.0.5", {"start": v(70, -90) * mm, "mid": v(77.07, -87.07) * mm, "end": v(80, -80) * mm});
            skLineSegment(sketch, "E95.0.6", {"start": v(80, -80) * mm, "end": v(80, 80) * mm});
            skArc(sketch, "E95.0.7", {"start": v(80, 80) * mm, "mid": v(77.07, 87.07) * mm, "end": v(70, 90) * mm});
            skSolve(sketch);
        }
        {
            var Q0;
            {var subQ1=sQuery(id+"F16.wireOp",EDGE,"E94.0");Q0=makeQuery(id+"F16.imprint","IMPRINT",FACE,{"disambiguationData":[TD([[makeQuery(id+"F16.imprint","IMPRINT",EDGE,{"derivedFrom":subQ1}),1.0]])]});}
            var Q1;
            Q1=makeQuery(id+"F16.imprint","IMPRINT",FACE,{"disambiguationData":[TD([[makeQuery(id+"F16.imprint","IMPRINT",EDGE,{"derivedFrom":sQuery(id+"F16.wireOp",EDGE,"E79")}),-1.0]])]});
            var Q2;
            Q2=makeQuery(id+"F16.imprint","IMPRINT",FACE,{"disambiguationData":[TD([[makeQuery(id+"F16.imprint","IMPRINT",EDGE,{"derivedFrom":sQuery(id+"F16.wireOp",EDGE,"E87.MirrorCS")}),-1.0]])]});
            var Q3;
            Q3=makeQuery(id+"F2.opExtrude","CAP_FACE",FACE,{"disambiguationData":[OSD([sQuery(id+"F0.wireOp",EDGE,"E12"),sQuery(id+"F0.wireOp",EDGE,"E13"),sQuery(id+"F0.wireOp",EDGE,"E14"),sQuery(id+"F0.wireOp",EDGE,"E15"),sQuery(id+"F0.wireOp",EDGE,"E17.filletArc"),sQuery(id+"F0.wireOp",EDGE,"E18.filletArc"),sQuery(id+"F0.wireOp",EDGE,"E19.filletArc"),sQuery(id+"F0.wireOp",EDGE,"E20.filletArc"),sQuery(id+"F0.wireOp",EDGE,"E25.0"),sQuery(id+"F0.wireOp",EDGE,"E25.1"),sQuery(id+"F0.wireOp",EDGE,"E25.2"),sQuery(id+"F0.wireOp",EDGE,"E25.3"),sQuery(id+"F0.wireOp",EDGE,"E25.4"),sQuery(id+"F0.wireOp",EDGE,"E25.5"),sQuery(id+"F0.wireOp",EDGE,"E25.6"),sQuery(id+"F0.wireOp",EDGE,"E25.7")])],"isStart":false});
            extrude(context, id + "F17", {"entities" : qUnion([Q0, Q1, Q2]), "endBound" : BoundingType.UP_TO_SURFACE, "depth" : 5 * mm, "endBoundEntityFace" : qUnion([Q3]), "offsetDistance" : 25 * mm});
        }
    });
